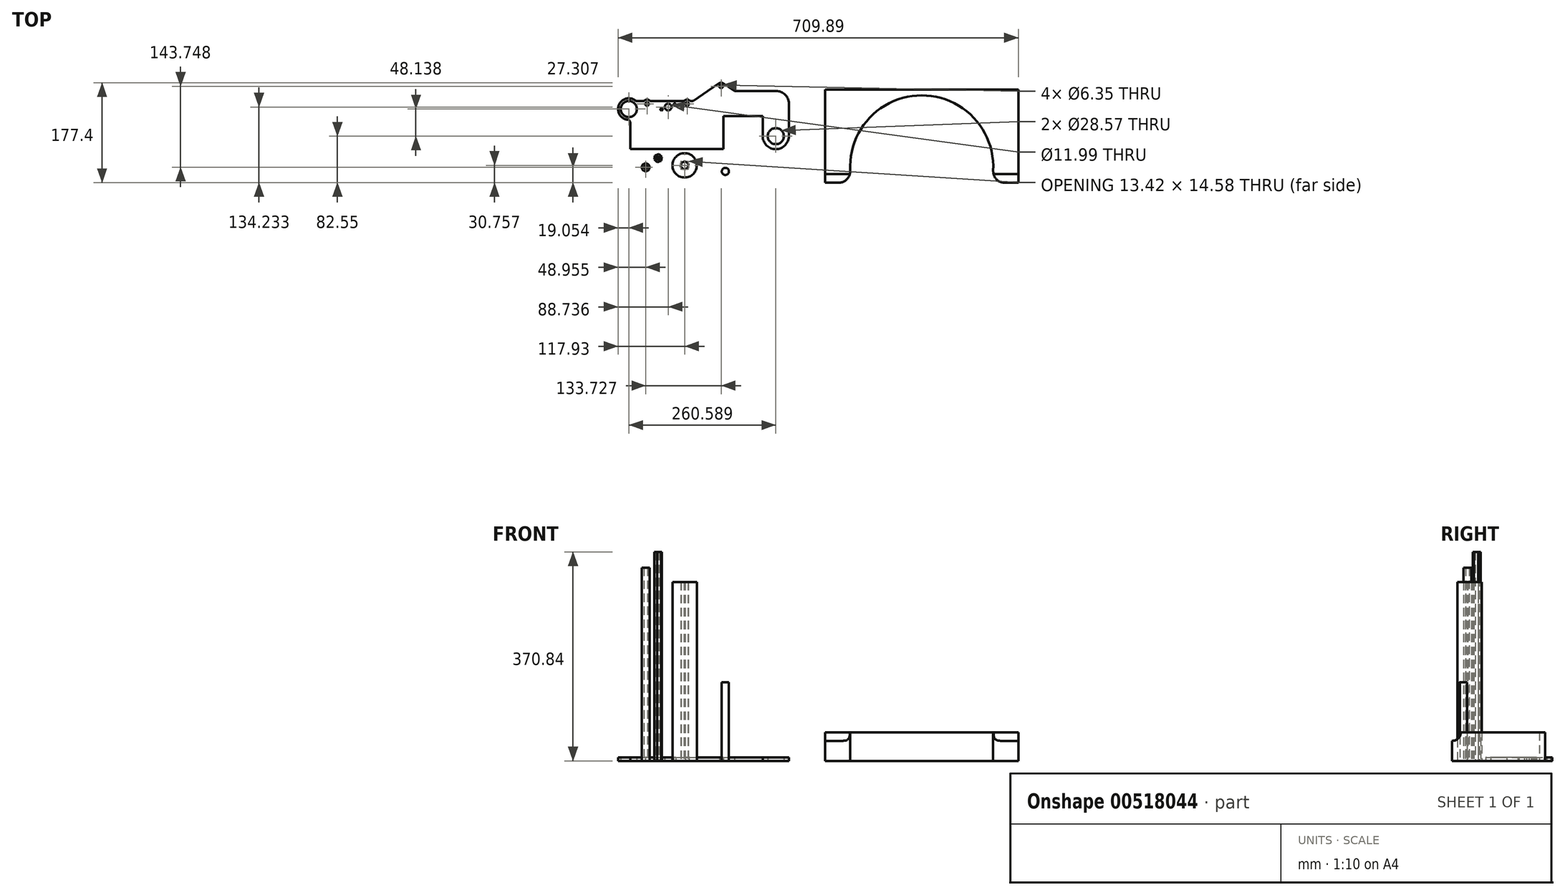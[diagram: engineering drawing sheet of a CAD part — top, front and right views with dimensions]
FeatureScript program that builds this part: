
annotation { "Feature Type Name" : "Feature", "Feature Type Description" : "" }
export const myFeature = defineFeature(function(context is Context, id is Id, definition is map)
    precondition{}
    {
        {
            assignVariable(context, id + "F0", {"name" : "inner_width", "anyValue" : 342.9 * mm});
        }
        {
            var Q0;
            Q0=qCreatedBy(makeId("Top.planeOp"),FACE);
            var sketch = newSketch(context, id + "F1", { "sketchPlane" : qUnion([Q0])});
            skCircle(sketch, "E0", {"center": v(-76.69, 48.14) * mm, "radius": 21.59 * mm, "construction": true});
            skCircle(sketch, "E1", {"center": v(-76.69, 48.14) * mm, "radius": 14.29 * mm});
            skArc(sketch, "E2", {"start": v(-63.83, 62.2) * mm, "mid": v(-94.85, 53.87) * mm, "end": v(-74.22, 29.25) * mm});
            skLineSegment(sketch, "E3", {"start": v(-74.22, 29.25) * mm, "end": v(-74.22, -22.94) * mm});
            skLineSegment(sketch, "E4", {"start": v(-74.22, -22.94) * mm, "end": v(90.88, -22.94) * mm});
            skLineSegment(sketch, "E5", {"start": v(90.88, -22.94) * mm, "end": v(90.88, 35.73) * mm});
            skLineSegment(sketch, "E6", {"start": v(184.86, 80.18) * mm, "end": v(110.56, 80.18) * mm});
            skLineSegment(sketch, "E7", {"start": v(-74.22, 14.56) * mm, "end": v(90.88, 14.56) * mm, "construction": true});
            skPoint(sketch, "E8.centerSnap0", {"position": v(205.18, 57.96) * mm});
            skArc(sketch, "E9", {"start": v(90.5, 93.76) * mm, "mid": v(86.94, 94.85) * mm, "end": v(83.38, 93.76) * mm});
            skLineSegment(sketch, "E10", {"start": v(83.38, 93.76) * mm, "end": v(63.33, 80.18) * mm});
            skLineSegment(sketch, "E11", {"start": v(90.5, 93.76) * mm, "end": v(110.56, 80.18) * mm});
            skCircle(sketch, "E12", {"center": v(86.94, 88.5) * mm, "radius": 3.18 * mm});
            skLineSegment(sketch, "E13", {"start": v(36.9, 62.2) * mm, "end": v(63.33, 80.18) * mm});
            skCircle(sketch, "E14", {"center": v(-7, 51.68) * mm, "radius": 6 * mm});
            skCircle(sketch, "E15", {"center": v(4.74, 55.96) * mm, "radius": 2 * mm});
            skLineSegment(sketch, "E16", {"start": v(4.74, 55.96) * mm, "end": v(-18.75, 47.4) * mm, "construction": true});
            skCircle(sketch, "E17", {"center": v(-18.75, 47.4) * mm, "radius": 2 * mm});
            skLineSegment(sketch, "E18", {"start": v(-7, 51.68) * mm, "end": v(3.74, 51.68) * mm, "construction": true});
            skCircle(sketch, "E19", {"center": v(-44.31, 57.12) * mm, "radius": 3.18 * mm});
            skCircle(sketch, "E20", {"center": v(26.72, 57.12) * mm, "radius": 3.18 * mm});
            skLineSegment(sketch, "E21", {"start": v(-63.83, 62.2) * mm, "end": v(-50, 62.2) * mm});
            skArc(sketch, "E22", {"start": v(-38.63, 62.2) * mm, "mid": v(-44.31, 64.74) * mm, "end": v(-50, 62.2) * mm});
            skArc(sketch, "E23", {"start": v(32.4, 62.2) * mm, "mid": v(26.72, 64.74) * mm, "end": v(21.04, 62.2) * mm});
            skLineSegment(sketch, "E24.trimOffspring", {"start": v(32.4, 62.2) * mm, "end": v(36.9, 62.2) * mm});
            skLineSegment(sketch, "E25.trimOffspring", {"start": v(-38.63, 62.2) * mm, "end": v(21.04, 62.2) * mm});
            skPoint(sketch, "E26.orphan", {"position": v(205.18, 35.73) * mm});
            skPoint(sketch, "E27.end.orphan", {"position": v(205.18, 80.18) * mm});
            skLineSegment(sketch, "E28", {"start": v(160.73, 35.73) * mm, "end": v(160.73, 0) * mm});
            skArc(sketch, "E29", {"start": v(184.86, 80.18) * mm, "mid": v(200.57, 73.67) * mm, "end": v(207.08, 57.96) * mm});
            skLineSegment(sketch, "E30", {"start": v(207.08, 57.96) * mm, "end": v(207.08, 0) * mm});
            skArc(sketch, "E31", {"start": v(160.73, 0) * mm, "mid": v(183.9, -23.18) * mm, "end": v(207.08, 0) * mm});
            skLineSegment(sketch, "E32", {"start": v(90.88, 35.73) * mm, "end": v(160.73, 35.73) * mm});
            skCircle(sketch, "E33", {"center": v(183.9, 0) * mm, "radius": 14.29 * mm});
            skSolve(sketch);
        }
        {
            var Q0;
            Q0=makeQuery(id+"F1.imprint","IMPRINT",FACE,{"disambiguationData":[TD([[makeQuery(id+"F1.imprint","IMPRINT",EDGE,{"derivedFrom":sQuery(id+"F1.wireOp",EDGE,"E1")}),-1.0]])]});
            var Q1;
            Q1=makeQuery(id+"F1.imprint","IMPRINT",FACE,{"disambiguationData":[TD([[makeQuery(id+"F1.imprint","IMPRINT",EDGE,{"derivedFrom":sQuery(id+"F1.wireOp",EDGE,"E19")}),-1.0]])]});
            var Q2;
            Q2=makeQuery(id+"F1.imprint","IMPRINT",FACE,{"disambiguationData":[TD([[makeQuery(id+"F1.imprint","IMPRINT",EDGE,{"derivedFrom":sQuery(id+"F1.wireOp",EDGE,"E20")}),-1.0]])]});
            extrude(context, id + "F2", {"entities" : qUnion([Q0, Q1, Q2]), "depth" : 6.35 * mm});
        }
        {
            var Q0;
            Q0=qCreatedBy(makeId("Top.planeOp"),FACE);
            var sketch = newSketch(context, id + "F3", { "sketchPlane" : qUnion([Q0])});
            skCircle(sketch, "E34", {"center": v(-46.78, -55.24) * mm, "radius": 6.99 * mm});
            skCircle(sketch, "E35", {"center": v(-46.78, -55.24) * mm, "radius": 3.18 * mm});
            skSolve(sketch);
        }
        {
            var Q0;
            Q0=qSketchRegion(id+"F3",true);
            extrude(context, id + "F4", {"entities" : qUnion([Q0]), "depth" : getVariable(context, 'inner_width')});
        }
        {
            var Q0;
            Q0=qCreatedBy(makeId("Top.planeOp"),FACE);
            var sketch = newSketch(context, id + "F5", { "sketchPlane" : qUnion([Q0])});
            skCircle(sketch, "E36.cCircle", {"center": v(-24.83, -39.03) * mm, "radius": 6.35 * mm, "construction": true});
            skLineSegment(sketch, "E36.0", {"start": v(-19.3, -43.86) * mm, "end": v(-26.24, -46.23) * mm});
            skLineSegment(sketch, "E36.1", {"start": v(-26.24, -46.23) * mm, "end": v(-31.77, -41.4) * mm});
            skLineSegment(sketch, "E36.2", {"start": v(-31.77, -41.4) * mm, "end": v(-30.35, -34.2) * mm});
            skLineSegment(sketch, "E36.3", {"start": v(-30.35, -34.2) * mm, "end": v(-23.4, -31.84) * mm});
            skLineSegment(sketch, "E36.4", {"start": v(-23.4, -31.84) * mm, "end": v(-17.89, -36.66) * mm});
            skLineSegment(sketch, "E36.5", {"start": v(-17.89, -36.66) * mm, "end": v(-19.3, -43.86) * mm});
            skPoint(sketch, "E36.0.midPoint", {"position": v(-22.77, -45.04) * mm});
            skCircle(sketch, "E37", {"center": v(-24.83, -39.03) * mm, "radius": 2.55 * mm});
            skSolve(sketch);
        }
        {
            var Q0;
            Q0=qSketchRegion(id+"F5",true);
            extrude(context, id + "F6", {"entities" : qUnion([Q0]), "depth" : getVariable(context, 'inner_width') + 27.94 * mm});
        }
        {
            var Q0;
            Q0=qCreatedBy(makeId("Top.planeOp"),FACE);
            var sketch = newSketch(context, id + "F7", { "sketchPlane" : qUnion([Q0])});
            skCircle(sketch, "E38", {"center": v(22.2, -51.8) * mm, "radius": 21.59 * mm});
            skCircle(sketch, "E39.cCircle", {"center": v(22.2, -51.8) * mm, "radius": 6.35 * mm, "construction": true});
            skLineSegment(sketch, "E39.0", {"start": v(28.1, -56.12) * mm, "end": v(21.4, -59.08) * mm});
            skLineSegment(sketch, "E39.1", {"start": v(21.4, -59.08) * mm, "end": v(15.48, -54.75) * mm});
            skLineSegment(sketch, "E39.2", {"start": v(15.48, -54.75) * mm, "end": v(16.27, -47.46) * mm});
            skLineSegment(sketch, "E39.3", {"start": v(16.27, -47.46) * mm, "end": v(22.98, -44.5) * mm});
            skLineSegment(sketch, "E39.4", {"start": v(22.98, -44.5) * mm, "end": v(28.9, -48.83) * mm});
            skLineSegment(sketch, "E39.5", {"start": v(28.9, -48.83) * mm, "end": v(28.1, -56.12) * mm});
            skPoint(sketch, "E39.0.midPoint", {"position": v(24.75, -57.6) * mm});
            skSolve(sketch);
        }
        {
            var Q0;
            Q0=makeQuery(id+"F7.imprint","IMPRINT",FACE,{"disambiguationData":[TD([[makeQuery(id+"F7.imprint","IMPRINT",EDGE,{"derivedFrom":sQuery(id+"F7.wireOp",EDGE,"E38")}),1.0]])]});
            extrude(context, id + "F8", {"entities" : qUnion([Q0]), "depth" : getVariable(context, 'inner_width') - 25.4 * mm});
        }
        {
            var Q0;
            Q0=qCreatedBy(makeId("Top.planeOp"),FACE);
            var sketch = newSketch(context, id + "F9", { "sketchPlane" : qUnion([Q0])});
            skLineSegment(sketch, "E40.bottom", {"start": v(271.25, 82.55) * mm, "end": v(614.15, 82.55) * mm});
            skLineSegment(sketch, "E40.top", {"start": v(271.25, -82.55) * mm, "end": v(318.81, -82.55) * mm});
            skLineSegment(sketch, "E40.left", {"start": v(271.25, 82.55) * mm, "end": v(271.25, -82.55) * mm});
            skLineSegment(sketch, "E40.right", {"start": v(614.15, 82.55) * mm, "end": v(614.15, -82.55) * mm});
            skPoint(sketch, "E40.middle", {"position": v(442.7, 0) * mm});
            skArc(sketch, "E41", {"start": v(566.6, -82.55) * mm, "mid": v(442.7, 72.4) * mm, "end": v(318.81, -82.55) * mm});
            skLineSegment(sketch, "E42.trimOffspring", {"start": v(566.6, -82.55) * mm, "end": v(614.15, -82.55) * mm});
            skSolve(sketch);
        }
        {
            var Q0;
            Q0=qSketchRegion(id+"F9",true);
            extrude(context, id + "F10", {"entities" : qUnion([Q0]), "depth" : 50.8 * mm});
        }
        {
            var Q0;
            Q0=makeQuery(id+"F10.opExtrude","SWEPT_EDGE",EDGE,{"disambiguationData":[OSD([sQuery(id+"F9.wireOp",EDGE,"E40.top"),sQuery(id+"F9.wireOp",EDGE,"E41")])]});
            var Q1;
            Q1=makeQuery(id+"F10.opExtrude","SWEPT_EDGE",EDGE,{"disambiguationData":[OSD([sQuery(id+"F9.wireOp",EDGE,"E41"),sQuery(id+"F9.wireOp",EDGE,"E42.trimOffspring")])]});
            fillet(context, id + "F11", {"entities" : qUnion([Q0, Q1]), "radius" : 20.32 * mm, "tangentPropagation" : true, "allowEdgeOverflow" : false});
        }
        {
            var Q0;
            Q0=makeQuery(id+"F10.opExtrude","SWEPT_FACE",FACE,{"disambiguationData":[OSD([sQuery(id+"F9.wireOp",EDGE,"E40.right")])]});
            var sketch = newSketch(context, id + "F12", { "sketchPlane" : qUnion([Q0])});
            skLineSegment(sketch, "E43.0.0", {"start": v(-82.55, 0) * mm, "end": v(82.55, 0) * mm});
            skLineSegment(sketch, "E43.0.1", {"start": v(82.55, 0) * mm, "end": v(82.55, 50.8) * mm});
            skLineSegment(sketch, "E43.0.2", {"start": v(82.55, 50.8) * mm, "end": v(-82.55, 50.8) * mm});
            skLineSegment(sketch, "E43.0.3", {"start": v(-82.55, 50.8) * mm, "end": v(-82.55, 0) * mm});
            skCircle(sketch, "E44", {"center": v(-82.55, 50.8) * mm, "radius": 15.24 * mm});
            skSolve(sketch);
        }
        {
            var Q0;
            {var subQ0=sQuery(id+"F12.wireOp",EDGE,"E43.0.3");var subQ1=sQuery(id+"F12.wireOp",EDGE,"E43.0.2");var subQ2=makeQuery(id+"F12.imprint","INTERSECT",VERTEX,{"derivedFrom":[subQ1,subQ0]});Q0=makeQuery(id+"F12.imprint","IMPRINT",FACE,{"disambiguationData":[TD([[makeQuery(id+"F12.imprint","IMPRINT",EDGE,{"disambiguationData":[TD([[subQ2,1.0]])],"derivedFrom":subQ1}),1.0]])]});}
            var Q1;
            Q1=makeQuery(id+"F10.opExtrude","SWEPT_FACE",FACE,{"disambiguationData":[OSD([sQuery(id+"F9.wireOp",EDGE,"E40.left")])]});
            extrude(context, id + "F13", {"entities" : qUnion([Q0]), "operationType" : NewBodyOperationType.REMOVE, "endBound" : BoundingType.UP_TO_SURFACE, "oppositeDirection" : true, "endBoundEntityFace" : qUnion([Q1]), "depth" : 25.4 * mm});
        }
        {
            var Q0;
            Q0=qCreatedBy(makeId("Top.planeOp"),FACE);
            var sketch = newSketch(context, id + "F14", { "sketchPlane" : qUnion([Q0])});
            skCircle(sketch, "E45", {"center": v(94.46, -62.59) * mm, "radius": 6.35 * mm});
            skSolve(sketch);
        }
        {
            var Q0;
            Q0=qSketchRegion(id+"F14",true);
            extrude(context, id + "F15", {"entities" : qUnion([Q0]), "depth" : 139.7 * mm});
        }
        {
            var Q0;
            Q0=makeQuery(id+"F2.opExtrude","SWEPT_EDGE",EDGE,{"disambiguationData":[OSD([sQuery(id+"F1.wireOp",EDGE,"E22"),sQuery(id+"F1.wireOp",EDGE,"E25.trimOffspring")])]});
            var Q1;
            Q1=makeQuery(id+"F2.opExtrude","SWEPT_EDGE",EDGE,{"disambiguationData":[OSD([sQuery(id+"F1.wireOp",EDGE,"E23"),sQuery(id+"F1.wireOp",EDGE,"E25.trimOffspring")])]});
            var Q2;
            Q2=makeQuery(id+"F2.opExtrude","SWEPT_EDGE",EDGE,{"disambiguationData":[OSD([sQuery(id+"F1.wireOp",EDGE,"E23"),sQuery(id+"F1.wireOp",EDGE,"E24.trimOffspring")])]});
            var Q3;
            Q3=makeQuery(id+"F2.opExtrude","SWEPT_EDGE",EDGE,{"disambiguationData":[OSD([sQuery(id+"F1.wireOp",EDGE,"E13"),sQuery(id+"F1.wireOp",EDGE,"E24.trimOffspring")])]});
            var Q4;
            Q4=makeQuery(id+"F2.opExtrude","SWEPT_EDGE",EDGE,{"disambiguationData":[OSD([sQuery(id+"F1.wireOp",EDGE,"E21"),sQuery(id+"F1.wireOp",EDGE,"E22")])]});
            var Q5;
            Q5=makeQuery(id+"F2.opExtrude","SWEPT_EDGE",EDGE,{"disambiguationData":[OSD([sQuery(id+"F1.wireOp",EDGE,"E2"),sQuery(id+"F1.wireOp",EDGE,"E21")])]});
            var Q6;
            Q6=makeQuery(id+"F2.opExtrude","SWEPT_EDGE",EDGE,{"disambiguationData":[OSD([sQuery(id+"F1.wireOp",EDGE,"E2"),sQuery(id+"F1.wireOp",EDGE,"E3")])]});
            fillet(context, id + "F16", {"entities" : qUnion([Q0, Q1, Q2, Q3, Q4, Q5, Q6]), "radius" : 5.08 * mm, "tangentPropagation" : true, "allowEdgeOverflow" : false});
        }
    });
